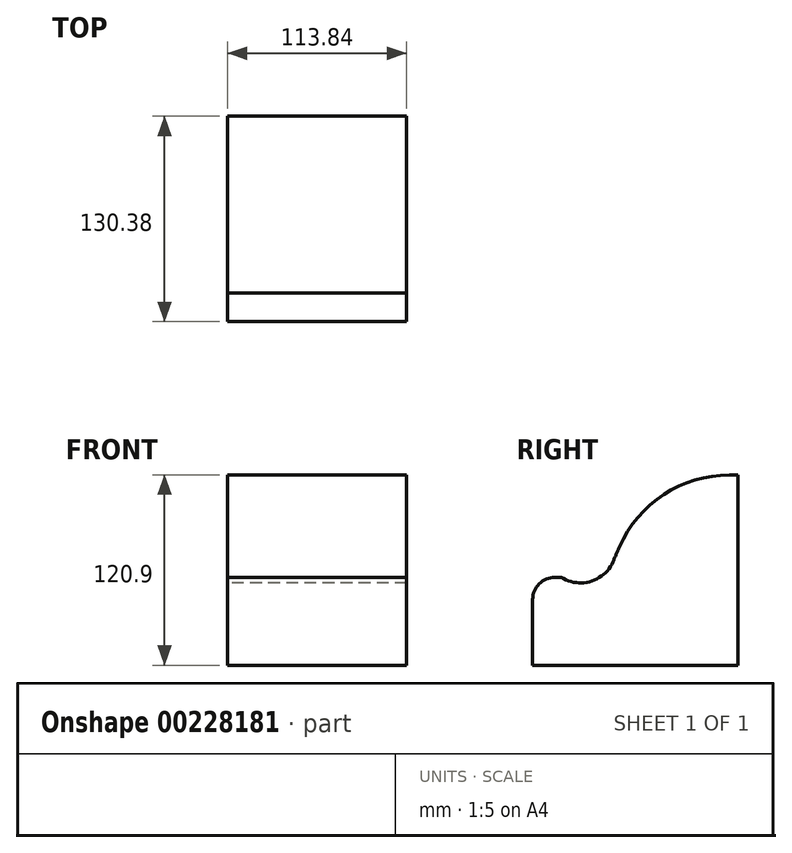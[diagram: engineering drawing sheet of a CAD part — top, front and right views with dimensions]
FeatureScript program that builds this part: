
annotation { "Feature Type Name" : "Feature", "Feature Type Description" : "" }
export const myFeature = defineFeature(function(context is Context, id is Id, definition is map)
    precondition{}
    {
        {
            var Q0;
            Q0=qCreatedBy(makeId("Top.planeOp"),FACE);
            var sketch = newSketch(context, id + "F0", { "sketchPlane" : qUnion([Q0])});
            skLineSegment(sketch, "E0.bottom", {"start": v(-56.92, 39.3) * mm, "end": v(56.92, 39.3) * mm});
            skLineSegment(sketch, "E0.top", {"start": v(-56.92, -42.31) * mm, "end": v(56.92, -42.31) * mm});
            skLineSegment(sketch, "E0.left", {"start": v(-56.92, 39.3) * mm, "end": v(-56.92, -42.31) * mm});
            skLineSegment(sketch, "E0.right", {"start": v(56.92, 39.3) * mm, "end": v(56.92, -42.31) * mm});
            skSolve(sketch);
        }
        {
            var Q0;
            Q0 = qSketchRegion(id + "F0", true);
            extrude(context, id + "F1", {"entities" : qUnion([Q0]), "depth" : 120.9 * mm});
        }
        {
            var Q0;
            Q0=makeQuery(id+"F1.opExtrude","CAP_EDGE",EDGE,{"disambiguationData":[OSD([sQuery(id+"F0.wireOp",EDGE,"E0.top")])],"isStart":false});
            fillet(context, id + "F2", {"entities" : qUnion([Q0]), "radius" : 76.2 * mm, "tangentPropagation" : true, "allowEdgeOverflow" : false});
        }
        {
            var Q0;
            Q0=makeQuery(id+"F1.opExtrude","SWEPT_FACE",FACE,{"disambiguationData":[OSD([sQuery(id+"F0.wireOp",EDGE,"E0.top")])]});
            extrude(context, id + "F3", {"entities" : qUnion([Q0]), "operationType" : NewBodyOperationType.ADD, "depth" : 48.77 * mm});
        }
        {
            var Q0;
            {var subQ0=sQuery(id+"F0.wireOp",EDGE,"E0.top");var subQ1=makeQuery(id+"F2.opFillet","BLEND_EDGE",EDGE,{"blendedFrom":[makeQuery(id+"F1.opExtrude","CAP_EDGE",EDGE,{"disambiguationData":[OSD([subQ0])],"isStart":false}),makeQuery(id+"F1.opExtrude","SWEPT_FACE",FACE,{"disambiguationData":[OSD([subQ0])]})],"blendedInto":[makeQuery(id+"F1.opExtrude","SWEPT_FACE",FACE,{"disambiguationData":[OSD([subQ0])]})]});Q0=makeQuery(id+"F3.boolean.opBoolean","MERGE",EDGE,{"derivedFrom":[subQ1,makeQuery(id+"F3.opExtrude","CAP_EDGE",EDGE,{"disambiguationData":[OSD([subQ0]),TDD([subQ1])],"isStart":true})]});}
            fillet(context, id + "F4", {"entities" : qUnion([Q0]), "radius" : 50.8 * mm, "tangentPropagation" : true, "rho" : .85, "crossSection" : FilletCrossSection.CONIC, "allowEdgeOverflow" : false});
        }
        {
            var Q0;
            {var subQ0=sQuery(id+"F0.wireOp",EDGE,"E0.top");Q0=makeQuery(id+"F3.opExtrude","SWEPT_FACE",FACE,{"disambiguationData":[OSD([subQ0]),TDD([makeQuery(id+"F2.opFillet","BLEND_EDGE",EDGE,{"blendedFrom":[makeQuery(id+"F1.opExtrude","CAP_EDGE",EDGE,{"disambiguationData":[OSD([subQ0])],"isStart":false}),makeQuery(id+"F1.opExtrude","SWEPT_FACE",FACE,{"disambiguationData":[OSD([subQ0])]})],"blendedInto":[makeQuery(id+"F1.opExtrude","SWEPT_FACE",FACE,{"disambiguationData":[OSD([subQ0])]})]})])]});}
            extrude(context, id + "F5", {"entities" : qUnion([Q0]), "operationType" : NewBodyOperationType.ADD, "depth" : 11.18 * mm});
        }
        {
            var Q0;
            {var subQ0=sQuery(id+"F0.wireOp",EDGE,"E0.top");var subQ1=makeQuery(id+"F2.opFillet","BLEND_EDGE",EDGE,{"blendedFrom":[makeQuery(id+"F1.opExtrude","CAP_EDGE",EDGE,{"disambiguationData":[OSD([subQ0])],"isStart":false}),makeQuery(id+"F1.opExtrude","SWEPT_FACE",FACE,{"disambiguationData":[OSD([subQ0])]})],"blendedInto":[makeQuery(id+"F1.opExtrude","SWEPT_FACE",FACE,{"disambiguationData":[OSD([subQ0])]})]});Q0=makeQuery(id+"F5.opExtrude","SWEPT_FACE",FACE,{"disambiguationData":[OSD([subQ0]),TDD([makeQuery(id+"F4.opFillet","BLEND_EDGE",EDGE,{"blendedFrom":[makeQuery(id+"F3.boolean.opBoolean","MERGE",EDGE,{"derivedFrom":[subQ1,makeQuery(id+"F3.opExtrude","CAP_EDGE",EDGE,{"disambiguationData":[OSD([subQ0]),TDD([subQ1])],"isStart":true})]}),makeQuery(id+"F3.opExtrude","SWEPT_FACE",FACE,{"disambiguationData":[OSD([subQ0]),TDD([subQ1])]})],"blendedInto":[makeQuery(id+"F3.opExtrude","SWEPT_FACE",FACE,{"disambiguationData":[OSD([subQ0]),TDD([subQ1])]})]})])]});}
            extrude(context, id + "F6", {"entities" : qUnion([Q0]), "operationType" : NewBodyOperationType.ADD, "depth" : 9.65 * mm});
        }
        {
            var Q0;
            {var subQ0=sQuery(id+"F0.wireOp",EDGE,"E0.top");Q0=makeQuery(id+"F6.boolean.opBoolean","INTERSECT",EDGE,{"derivedFrom":[makeQuery(id+"F4.opFillet","BLEND_FACE",FACE,{"disambiguationData":[OSD([subQ0])]}),makeQuery(id+"F6.opExtrude","CAP_FACE",FACE,{"disambiguationData":[OSD([subQ0])],"isStart":false})]});}
            fillet(context, id + "F7", {"entities" : qUnion([Q0]), "radius" : 22.56 * mm, "tangentPropagation" : true, "allowEdgeOverflow" : false});
        }
        {
            var Q0;
            {var subQ0=sQuery(id+"F0.wireOp",EDGE,"E0.top");Q0=makeQuery(id+"F5.opExtrude","CAP_EDGE",EDGE,{"disambiguationData":[OSD([subQ0]),TDD([makeQuery(id+"F3.opExtrude","CAP_EDGE",EDGE,{"disambiguationData":[OSD([subQ0]),TDD([makeQuery(id+"F2.opFillet","BLEND_EDGE",EDGE,{"blendedFrom":[makeQuery(id+"F1.opExtrude","CAP_EDGE",EDGE,{"disambiguationData":[OSD([subQ0])],"isStart":false}),makeQuery(id+"F1.opExtrude","SWEPT_FACE",FACE,{"disambiguationData":[OSD([subQ0])]})],"blendedInto":[makeQuery(id+"F1.opExtrude","SWEPT_FACE",FACE,{"disambiguationData":[OSD([subQ0])]})]})])],"isStart":false})])],"isStart":false});}
            fillet(context, id + "F8", {"entities" : qUnion([Q0]), "radius" : 14.1 * mm, "tangentPropagation" : true, "allowEdgeOverflow" : false});
        }
    });
